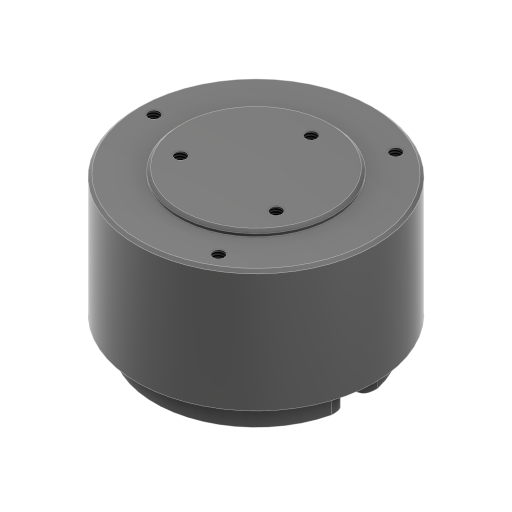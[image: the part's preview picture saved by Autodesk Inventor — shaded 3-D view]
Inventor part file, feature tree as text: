
AUTODESK INVENTOR PART (.ipt)
format: ipt  version: 2023 (Build 270158000, 158)  size: 230,400 bytes
history: native  units: in
note: dims shown in document units (in); Inventor stores cm internally (conversion verified against a paired STEP export)
features: sketch x5, hole x4, other x1, revolve x1, extrude x1
ambient origin geometry x8: Origin, YZ Plane, XZ Plane, XY Plane, X Axis, Y Axis, Z Axis, Center Point
bodies: Body1 (feature_tree)
feature tree (12):
  other  "ソリッド1"
  revolve  "回転1"
  hole  "穴1"  [1 undecoded]
  hole  "穴2"  [1 undecoded]
  sketch  "スケッチ4"
  hole  "穴3"  [1 undecoded]
  hole  "穴4"  [1 undecoded]
  extrude  "押し出し1"  Depth=0.0197in
  sketch  "スケッチ1"
  sketch  "スケッチ2"
  sketch  "スケッチ3"
  sketch  "スケッチ5"
note: 4 required parameter values undecoded (feature->parameter linkage not recoverable at this tier; creation-order binding heuristic only, values carry confidence <= 0.55)
